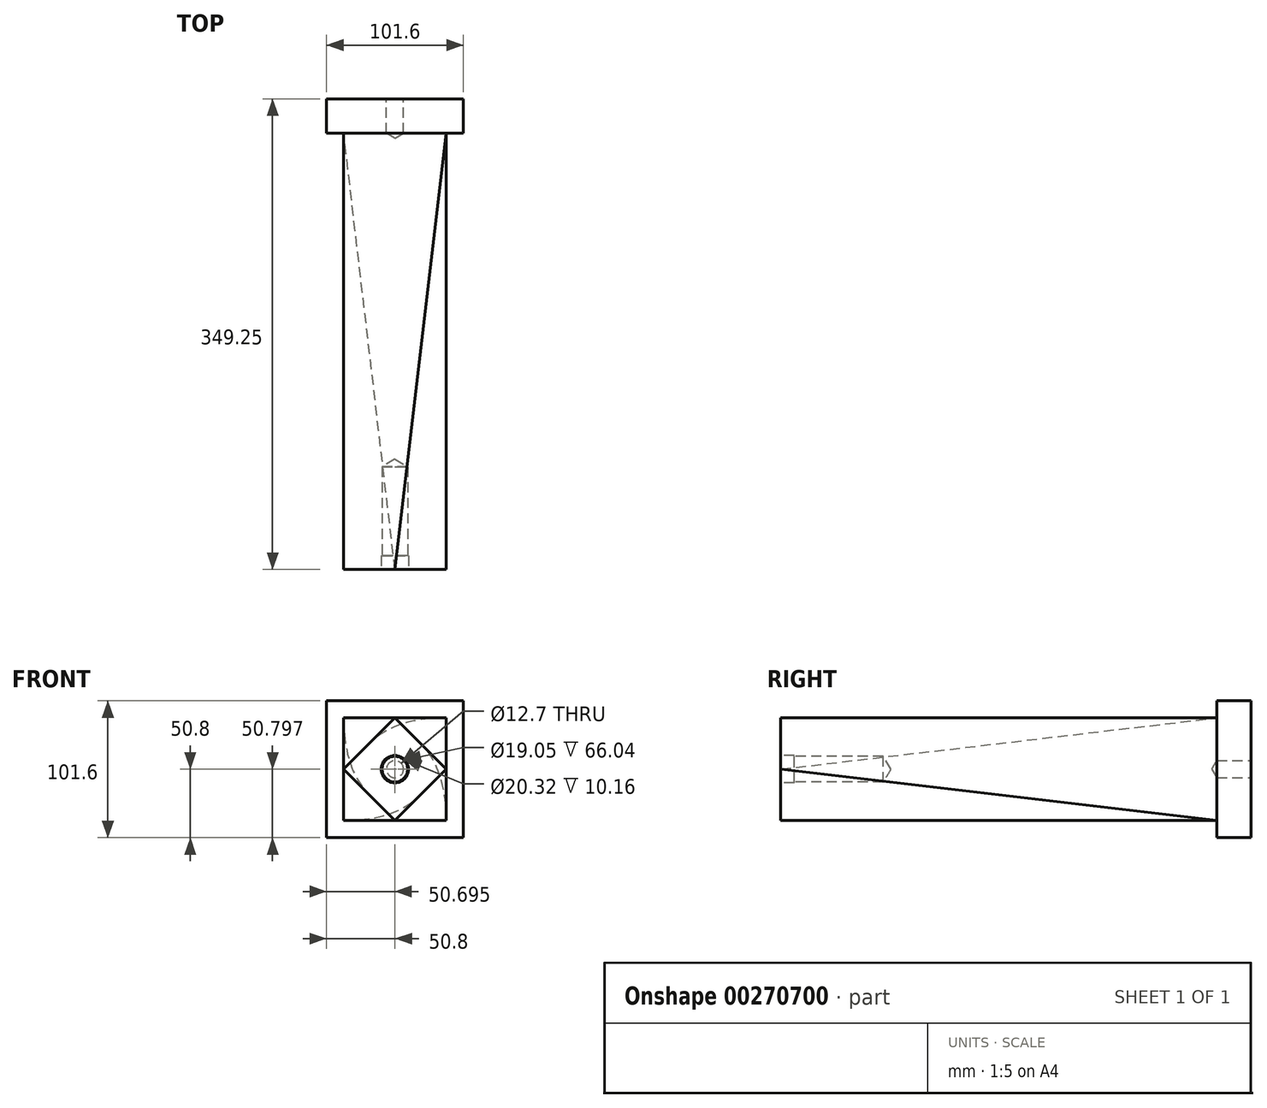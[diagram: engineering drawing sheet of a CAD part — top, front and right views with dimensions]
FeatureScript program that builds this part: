
annotation { "Feature Type Name" : "Feature", "Feature Type Description" : "" }
export const myFeature = defineFeature(function(context is Context, id is Id, definition is map)
    precondition{}
    {
        {
            var Q0;
            Q0=qCreatedBy(makeId("Front.planeOp"),FACE);
            var sketch = newSketch(context, id + "F0", { "sketchPlane" : qUnion([Q0])});
            skLineSegment(sketch, "E0.bottom", {"start": v(0, 0) * mm, "end": v(101.6, 0) * mm});
            skLineSegment(sketch, "E0.top", {"start": v(0, 101.6) * mm, "end": v(101.6, 101.6) * mm});
            skLineSegment(sketch, "E0.left", {"start": v(0, 0) * mm, "end": v(0, 101.6) * mm});
            skLineSegment(sketch, "E0.right", {"start": v(101.6, 0) * mm, "end": v(101.6, 101.6) * mm});
            skSolve(sketch);
        }
        {
            var Q0;
            Q0 = qSketchRegion(id + "F0", true);
            extrude(context, id + "F1", {"entities" : qUnion([Q0]), "depth" : 25.4 * mm});
        }
        {
            var Q0;
            Q0=makeQuery(id+"F1.opExtrude","CAP_FACE",FACE,{"disambiguationData":[OSD([sQuery(id+"F0.wireOp",EDGE,"E0.bottom"),sQuery(id+"F0.wireOp",EDGE,"E0.top"),sQuery(id+"F0.wireOp",EDGE,"E0.left"),sQuery(id+"F0.wireOp",EDGE,"E0.right")])],"isStart":false});
            var sketch = newSketch(context, id + "F2", { "sketchPlane" : qUnion([Q0])});
            skPoint(sketch, "E1.endSnap0", {"position": v(101.6, 50.8) * mm});
            skLineSegment(sketch, "E2.bottom", {"start": v(88.9, 88.9) * mm, "end": v(12.7, 88.9) * mm});
            skLineSegment(sketch, "E2.top", {"start": v(88.9, 12.7) * mm, "end": v(12.7, 12.7) * mm});
            skLineSegment(sketch, "E2.left", {"start": v(88.9, 88.9) * mm, "end": v(88.9, 12.7) * mm});
            skLineSegment(sketch, "E2.right", {"start": v(12.7, 88.9) * mm, "end": v(12.7, 12.7) * mm});
            skPoint(sketch, "E2.middle", {"position": v(50.8, 50.8) * mm});
            skLineSegment(sketch, "E3.bottom", {"start": v(0, 0) * mm, "end": v(101.6, 0) * mm});
            skLineSegment(sketch, "E3.top", {"start": v(0, 101.6) * mm, "end": v(101.6, 101.6) * mm});
            skLineSegment(sketch, "E3.left", {"start": v(0, 0) * mm, "end": v(0, 101.6) * mm});
            skLineSegment(sketch, "E3.right", {"start": v(101.6, 0) * mm, "end": v(101.6, 101.6) * mm});
            skSolve(sketch);
        }
        {
            var Q0;
            Q0=makeQuery(id+"F2.imprint","IMPRINT",FACE,{"disambiguationData":[TD([[makeQuery(id+"F2.imprint","IMPRINT",EDGE,{"derivedFrom":sQuery(id+"F2.wireOp",EDGE,"E2.bottom")}),-1.0]])]});
            cPlane(context, id + "F3", {"entities" : qUnion([Q0]), "cplaneType" : CPlaneType.OFFSET, "offset" : 323.85 * mm, "width" : 152.4 * mm, "height" : 152.4 * mm});
        }
        {
            var Q0;
            Q0=qCreatedBy(id+"F3.planeOp",FACE);
            var sketch = newSketch(context, id + "F4", { "sketchPlane" : qUnion([Q0])});
            skLineSegment(sketch, "E4", {"start": v(12.7, 50.8) * mm, "end": v(50.8, 88.9) * mm});
            skLineSegment(sketch, "E5", {"start": v(50.8, 12.7) * mm, "end": v(88.9, 50.8) * mm});
            skLineSegment(sketch, "E6", {"start": v(88.9, 50.8) * mm, "end": v(50.8, 88.9) * mm});
            skLineSegment(sketch, "E7", {"start": v(50.8, 12.7) * mm, "end": v(12.7, 50.8) * mm});
            skPoint(sketch, "E8.orphan", {"position": v(12.7, 88.9) * mm});
            skPoint(sketch, "E9.0.start.orphan", {"position": v(88.9, 88.9) * mm});
            skPoint(sketch, "E10.0.end.orphan", {"position": v(88.9, 12.7) * mm});
            skPoint(sketch, "E11.0.end.orphan", {"position": v(12.7, 12.7) * mm});
            skSolve(sketch);
        }
        {
            var Q1;
            Q1=makeQuery(id+"F4.imprint","IMPRINT",FACE,{"disambiguationData":[TD([[makeQuery(id+"F4.imprint","IMPRINT",EDGE,{"derivedFrom":sQuery(id+"F4.wireOp",EDGE,"E4")}),-1.0]])]});
            var Q2;
            Q2=makeQuery(id+"F2.imprint","IMPRINT",FACE,{"disambiguationData":[TD([[makeQuery(id+"F2.imprint","IMPRINT",EDGE,{"derivedFrom":sQuery(id+"F2.wireOp",EDGE,"E2.bottom")}),1.0]])]});
            loft(context, id + "F5", {"operationType" : NewBodyOperationType.ADD, "sheetProfilesArray" : [{ "sheetProfileEntities" : qUnion([Q1]) }, { "sheetProfileEntities" : qUnion([Q2]) }]});
        }
        {
            var Q0;
            Q0=makeQuery(id+"F1.opExtrude","CAP_FACE",FACE,{"disambiguationData":[OSD([sQuery(id+"F0.wireOp",EDGE,"E0.bottom"),sQuery(id+"F0.wireOp",EDGE,"E0.top"),sQuery(id+"F0.wireOp",EDGE,"E0.left"),sQuery(id+"F0.wireOp",EDGE,"E0.right")])],"isStart":true});
            var sketch = newSketch(context, id + "F6", { "sketchPlane" : qUnion([Q0])});
            skPoint(sketch, "E12", {"position": v(-50.8, 50.8) * mm});
            skSolve(sketch);
        }
        {
            var Q0;
            Q0=sQuery(id+"F6.wireOp",VERTEX,"E12");
            var Q1;
            Q1=makeQuery(id+"F1.opExtrude","SWEPT_BODY",BODY,{"disambiguationData":[OSD([sQuery(id+"F0.wireOp",EDGE,"E0.bottom"),sQuery(id+"F0.wireOp",EDGE,"E0.top"),sQuery(id+"F0.wireOp",EDGE,"E0.left"),sQuery(id+"F0.wireOp",EDGE,"E0.right")])]});
            hole(context, id + "F7", {"style" : HoleStyle.SIMPLE, "endStyle" : HoleEndStyle.BLIND, "holeDiameter" : 12.7 * mm, "holeDepth" : 25.4 * mm, "tappedDepth" : 12.7 * mm, "tapClearance" : 3, "locations" : qUnion([Q0]), "scope" : qUnion([Q1])});
        }
        {
            var Q0;
            Q0=makeQuery(id+"F4.imprint","IMPRINT",FACE,{"disambiguationData":[TD([[makeQuery(id+"F4.imprint","IMPRINT",EDGE,{"derivedFrom":sQuery(id+"F4.wireOp",EDGE,"E4")}),-1.0]])]});
            var sketch = newSketch(context, id + "F8", { "sketchPlane" : qUnion([Q0])});
            skPoint(sketch, "E13", {"position": v(31.76, 70.05) * mm});
            skPoint(sketch, "E14", {"position": v(69.63, 31.54) * mm});
            skPoint(sketch, "E15", {"position": v(50.7, 50.8) * mm});
            skSolve(sketch);
        }
        {
            var Q0;
            Q0=sQuery(id+"F8.wireOp",VERTEX,"E15");
            var Q1;
            Q1=makeQuery(id+"F1.opExtrude","SWEPT_BODY",BODY,{"disambiguationData":[OSD([sQuery(id+"F0.wireOp",EDGE,"E0.bottom"),sQuery(id+"F0.wireOp",EDGE,"E0.top"),sQuery(id+"F0.wireOp",EDGE,"E0.left"),sQuery(id+"F0.wireOp",EDGE,"E0.right")])]});
            hole(context, id + "F9", {"style" : HoleStyle.C_BORE, "endStyle" : HoleEndStyle.BLIND, "holeDiameter" : 19.05 * mm, "cBoreDiameter" : 20.32 * mm, "cBoreDepth" : 10.16 * mm, "holeDepth" : 76.2 * mm, "tappedDepth" : 12.7 * mm, "tapClearance" : 3, "locations" : qUnion([Q0]), "scope" : qUnion([Q1])});
        }
    });
